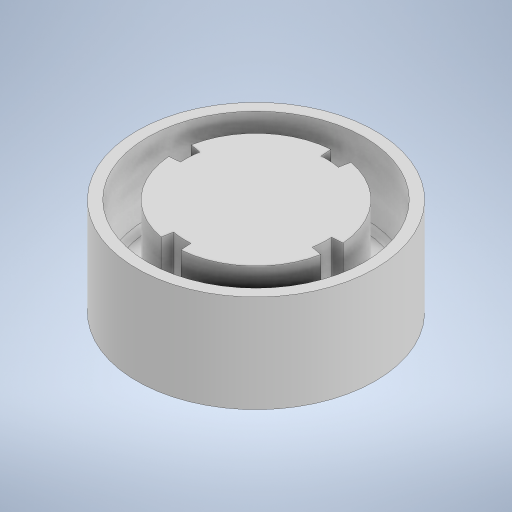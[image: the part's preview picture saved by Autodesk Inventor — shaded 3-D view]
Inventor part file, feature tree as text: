
AUTODESK INVENTOR PART (.ipt)
format: ipt  version: 2023.5 (Build 275446000, 446)  size: 266,240 bytes
history: native  units: mm
features: extrude x3, sketch x2, other x1, fillet x1, projected_geometry x1
ambient origin geometry x8: Origin, YZ Plane, XZ Plane, XY Plane, X Axis, Y Axis, Z Axis, Center Point
bodies: Body1 (feature_tree)
feature tree (8):
  other  "Bryła1"
  sketch  "Szkic1"
  extrude  "Wyciągnięcie proste1"  Depth=20.0mm
  extrude  "Wyciągnięcie proste2"  Depth=1.0mm
  extrude  "Wyciągnięcie proste3"  Depth=7.0mm TaperAngle=0.0deg
  fillet  "Zaokrąglenie1"  Radius=2.0mm
  sketch  "Szkic2"
  projected_geometry  "Pętla rzutowana1"
